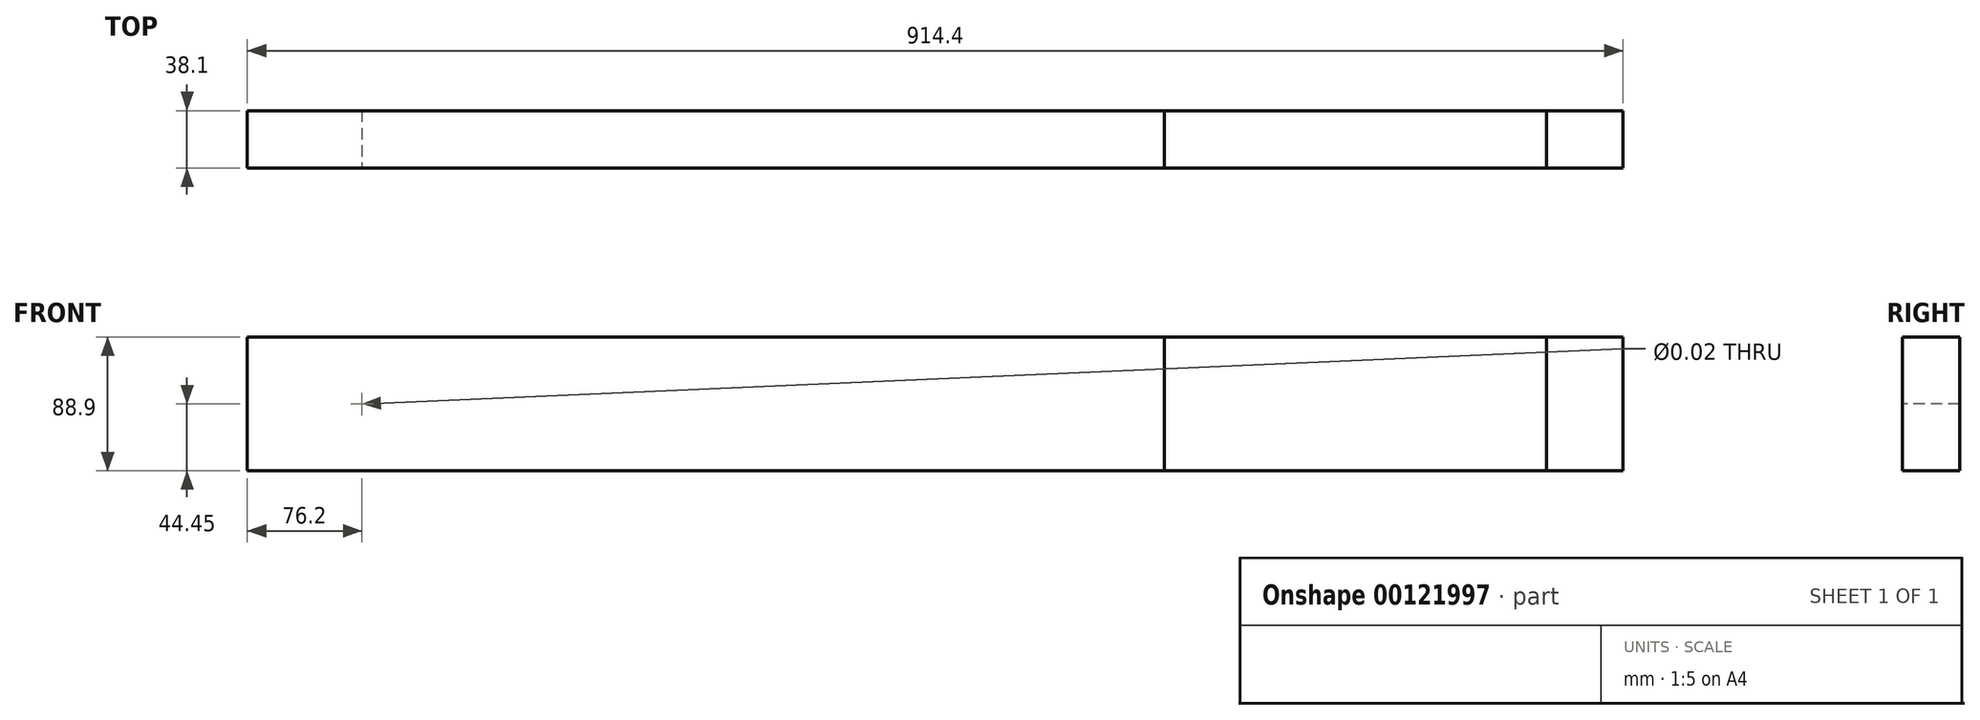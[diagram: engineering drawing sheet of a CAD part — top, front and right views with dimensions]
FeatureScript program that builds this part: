
annotation { "Feature Type Name" : "Feature", "Feature Type Description" : "" }
export const myFeature = defineFeature(function(context is Context, id is Id, definition is map)
    precondition{}
    {
        {
            var Q0;
            Q0=qCreatedBy(makeId("Right.planeOp"),FACE);
            var sketch = newSketch(context, id + "F0", { "sketchPlane" : qUnion([Q0])});
            skLineSegment(sketch, "E0.bottom", {"start": v(19.05, 44.45) * mm, "end": v(-19.05, 44.45) * mm});
            skLineSegment(sketch, "E0.top", {"start": v(19.05, -44.45) * mm, "end": v(-19.05, -44.45) * mm});
            skLineSegment(sketch, "E0.left", {"start": v(19.05, 44.45) * mm, "end": v(19.05, -44.45) * mm});
            skLineSegment(sketch, "E0.right", {"start": v(-19.05, 44.45) * mm, "end": v(-19.05, -44.45) * mm});
            skPoint(sketch, "E0.middle", {"position": v(0, 0) * mm});
            skSolve(sketch);
        }
        {
            var Q0;
            Q0=makeQuery(id+"F0.imprint","IMPRINT",FACE,{"disambiguationData":[TD([[makeQuery(id+"F0.imprint","IMPRINT",EDGE,{"derivedFrom":sQuery(id+"F0.wireOp",EDGE,"E0.bottom")}),1.0]])]});
            extrude(context, id + "F1", {"entities" : qUnion([Q0]), "depth" : 152.4 * mm});
        }
        {
            var Q0;
            Q0=makeQuery(id+"F1.opExtrude","SWEPT_FACE",FACE,{"disambiguationData":[OSD([sQuery(id+"F0.wireOp",EDGE,"E0.right")])]});
            var sketch = newSketch(context, id + "F2", { "sketchPlane" : qUnion([Q0])});
            skLineSegment(sketch, "E1", {"start": v(0, 0) * mm, "end": v(152.4, 0) * mm, "construction": true});
            skPoint(sketch, "E2", {"position": v(76.2, 0) * mm});
            skSolve(sketch);
        }
        {
            var Q0;
            Q0=sQuery(id+"F2.wireOp",VERTEX,"E2");
            var Q1;
            Q1=makeQuery(id+"F1.opExtrude","SWEPT_BODY",BODY,{"disambiguationData":[OSD([sQuery(id+"F0.wireOp",EDGE,"E0.bottom"),sQuery(id+"F0.wireOp",EDGE,"E0.top"),sQuery(id+"F0.wireOp",EDGE,"E0.left"),sQuery(id+"F0.wireOp",EDGE,"E0.right")])]});
            hole(context, id + "F3", {"style" : HoleStyle.SIMPLE, "endStyle" : HoleEndStyle.THROUGH, "standardTappedOrClearance" : lookupTablePath({ "standard" : "ANSI", "size" : "1/2 (0.5)", "type" : "Drilled" }), "standardBlindInLast" : lookupTablePath({ "standard" : "ANSI", "size" : "1/2", "type" : "Drilled" }), "holeDiameter" : 1 / 50.8 * mm, "locations" : qUnion([Q0]), "scope" : qUnion([Q1]), "isTappedThrough" : true});
        }
        {
            var Q0;
            Q0=makeQuery(id+"F1.opExtrude","CAP_FACE",FACE,{"disambiguationData":[OSD([sQuery(id+"F0.wireOp",EDGE,"E0.bottom"),sQuery(id+"F0.wireOp",EDGE,"E0.top"),sQuery(id+"F0.wireOp",EDGE,"E0.left"),sQuery(id+"F0.wireOp",EDGE,"E0.right")])],"isStart":false});
            extrude(context, id + "F4", {"entities" : qUnion([Q0]), "operationType" : NewBodyOperationType.ADD, "depth" : 711.2 * mm});
        }
        {
            var Q0;
            Q0 = qSketchRegion(id + "F0", true);
            extrude(context, id + "F5", {"entities" : qUnion([Q0]), "depth" : 914.4 * mm});
        }
        {
            var Q0;
            Q0 = qSketchRegion(id + "F0", true);
            extrude(context, id + "F6", {"entities" : qUnion([Q0]), "depth" : 609.6 * mm});
        }
    });
